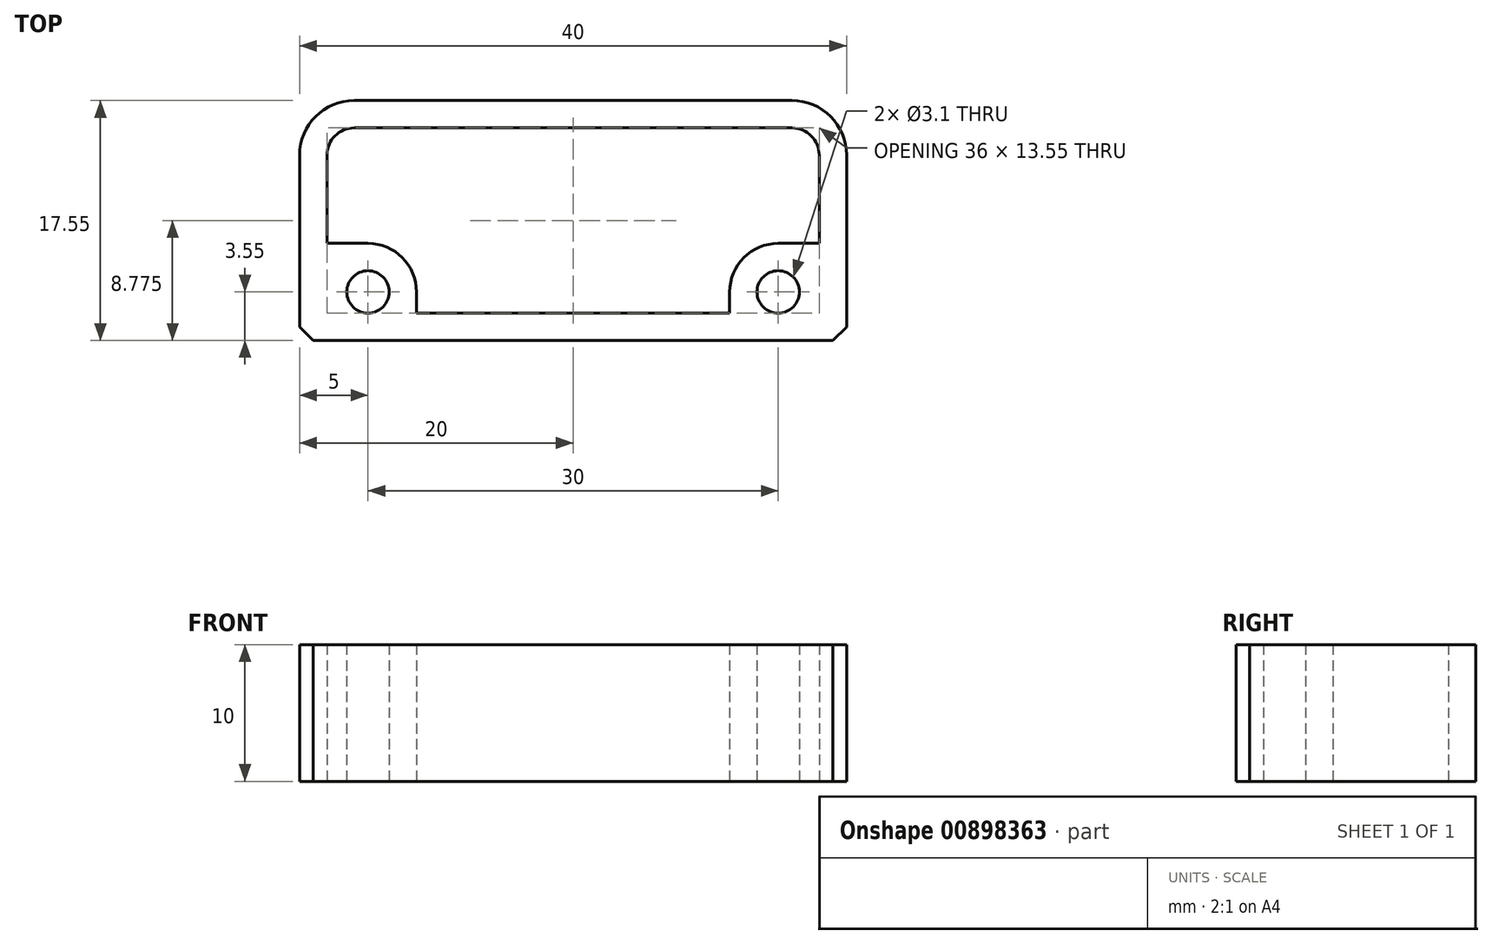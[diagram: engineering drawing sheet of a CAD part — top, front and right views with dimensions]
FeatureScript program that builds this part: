
annotation { "Feature Type Name" : "Feature", "Feature Type Description" : "" }
export const myFeature = defineFeature(function(context is Context, id is Id, definition is map)
    precondition{}
    {
        {
            var Q0;
            Q0=qCreatedBy(makeId("Top.planeOp"),FACE);
            var sketch = newSketch(context, id + "F0", { "sketchPlane" : qUnion([Q0])});
            skLineSegment(sketch, "E0", {"start": v(0, 0) * mm, "end": v(0, 29.32) * mm, "construction": true});
            skLineSegment(sketch, "E1", {"start": v(0, 0) * mm, "end": v(28.83, 0) * mm, "construction": true});
            skLineSegment(sketch, "E2", {"start": v(0, 17.55) * mm, "end": v(16, 17.55) * mm});
            skLineSegment(sketch, "E3", {"start": v(20, 13.55) * mm, "end": v(20, 0) * mm});
            skCircle(sketch, "E4", {"center": v(15, 3.55) * mm, "radius": 1.55 * mm});
            skPoint(sketch, "E5.visualSharp", {"position": v(20, 17.55) * mm});
            skArc(sketch, "E5.filletArc", {"start": v(20, 13.55) * mm, "mid": v(18.83, 16.38) * mm, "end": v(16, 17.55) * mm});
            skLineSegment(sketch, "E6.0", {"start": v(18, 13.55) * mm, "end": v(18, 7.1) * mm});
            skLineSegment(sketch, "E6.1", {"start": v(0, 15.55) * mm, "end": v(16, 15.55) * mm});
            skArc(sketch, "E7.0", {"start": v(18, 13.55) * mm, "mid": v(17.41, 14.96) * mm, "end": v(16, 15.55) * mm});
            skArc(sketch, "E8", {"start": v(15, 7.1) * mm, "mid": v(12.49, 6.06) * mm, "end": v(11.45, 3.55) * mm});
            skLineSegment(sketch, "E9", {"start": v(15, 7.1) * mm, "end": v(18, 7.1) * mm});
            skLineSegment(sketch, "E10", {"start": v(11.45, 3.55) * mm, "end": v(11.45, 2) * mm});
            skLineSegment(sketch, "E11", {"start": v(11.45, 2) * mm, "end": v(0, 2) * mm});
            skLineSegment(sketch, "E12", {"start": v(20, 0) * mm, "end": v(0, 0) * mm});
            skLineSegment(sketch, "E13", {"start": v(0, 17.55) * mm, "end": v(0, 15.55) * mm});
            skLineSegment(sketch, "E14", {"start": v(0, 0) * mm, "end": v(0, 2) * mm});
            skSolve(sketch);
        }
        {
            var Q0;
            Q0=qSketchRegion(id+"F0",true);
            extrude(context, id + "F1", {"entities" : qUnion([Q0]), "depth" : 10 * mm, "offsetDistance" : 25 * mm});
        }
        {
            var Q0;
            Q0=makeQuery(id+"F1.opExtrude","SWEPT_BODY",BODY,{"disambiguationData":[OSD([sQuery(id+"F0.wireOp",EDGE,"E2"),sQuery(id+"F0.wireOp",EDGE,"E3"),sQuery(id+"F0.wireOp",EDGE,"E4"),sQuery(id+"F0.wireOp",EDGE,"E5.filletArc"),sQuery(id+"F0.wireOp",EDGE,"E6.0"),sQuery(id+"F0.wireOp",EDGE,"E6.1"),sQuery(id+"F0.wireOp",EDGE,"E7.0"),sQuery(id+"F0.wireOp",EDGE,"E8"),sQuery(id+"F0.wireOp",EDGE,"E9"),sQuery(id+"F0.wireOp",EDGE,"E10"),sQuery(id+"F0.wireOp",EDGE,"E11"),sQuery(id+"F0.wireOp",EDGE,"E12"),sQuery(id+"F0.wireOp",EDGE,"E13"),sQuery(id+"F0.wireOp",EDGE,"E14")])]});
            var Q1;
            Q1=makeQuery(id+"F1.opExtrude","SWEPT_FACE",FACE,{"disambiguationData":[OSD([sQuery(id+"F0.wireOp",EDGE,"E13")])]});
            mirror(context, id + "F2", {"operationType" : NewBodyOperationType.ADD, "entities" : qUnion([Q0]), "mirrorPlane" : qUnion([Q1])});
        }
        {
            var Q0;
            Q0=makeQuery(id+"F2.opPattern","COPY",EDGE,{"derivedFrom":makeQuery(id+"F1.opExtrude","SWEPT_EDGE",EDGE,{"disambiguationData":[OSD([sQuery(id+"F0.wireOp",EDGE,"E3"),sQuery(id+"F0.wireOp",EDGE,"E12")])]}),"instanceName":"1"});
            var Q1;
            Q1=makeQuery(id+"F1.opExtrude","SWEPT_EDGE",EDGE,{"disambiguationData":[OSD([sQuery(id+"F0.wireOp",EDGE,"E3"),sQuery(id+"F0.wireOp",EDGE,"E12")])]});
            chamfer(context, id + "F3", {"entities" : qUnion([Q0, Q1]), "width" : 1 * mm, "tangentPropagation" : true});
        }
    });
